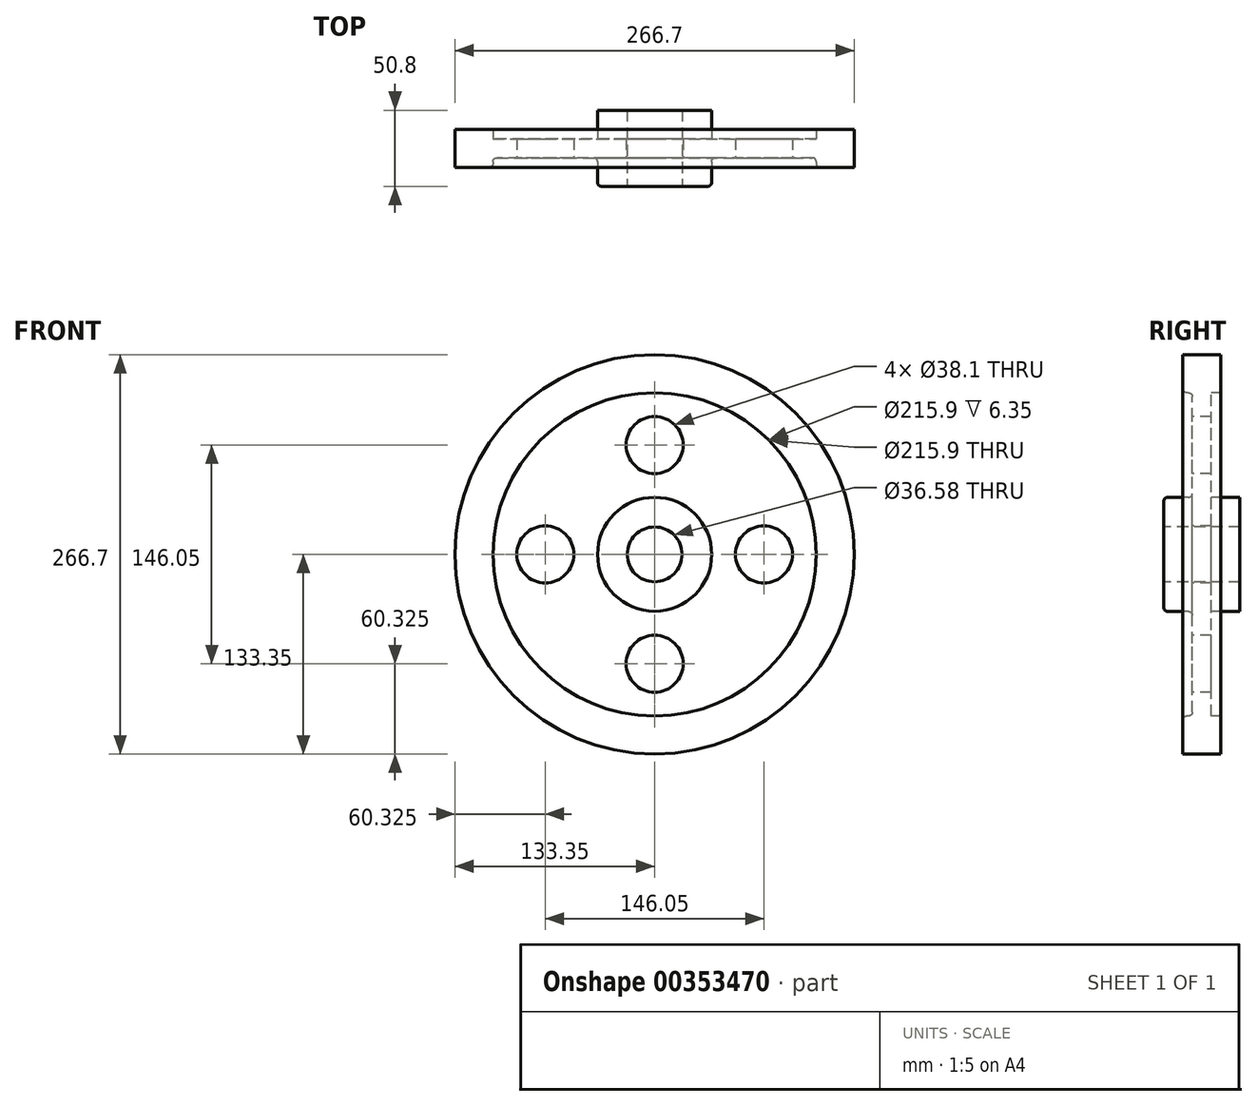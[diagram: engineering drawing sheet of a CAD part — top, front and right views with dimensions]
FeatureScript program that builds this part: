
annotation { "Feature Type Name" : "Feature", "Feature Type Description" : "" }
export const myFeature = defineFeature(function(context is Context, id is Id, definition is map)
    precondition{}
    {
        {
            var Q0;
            Q0=qCreatedBy(makeId("Right.planeOp"),FACE);
            var sketch = newSketch(context, id + "F0", { "sketchPlane" : qUnion([Q0])});
            skLineSegment(sketch, "E0", {"start": v(0, 0) * mm, "end": v(76.21, 0) * mm, "construction": true});
            skLineSegment(sketch, "E1.0", {"start": v(0, 18.29) * mm, "end": v(25.4, 18.29) * mm});
            skLineSegment(sketch, "E2.0", {"start": v(6.35, 38.1) * mm, "end": v(25.4, 38.1) * mm});
            skLineSegment(sketch, "E3.0", {"start": v(6.35, 107.95) * mm, "end": v(12.7, 107.95) * mm});
            skLineSegment(sketch, "E4.0", {"start": v(0, 133.35) * mm, "end": v(12.7, 133.35) * mm});
            skLineSegment(sketch, "E5", {"start": v(0, 0) * mm, "end": v(0, 133.35) * mm, "construction": true});
            skLineSegment(sketch, "E6.0", {"start": v(25.4, 18.29) * mm, "end": v(25.4, 38.1) * mm});
            skLineSegment(sketch, "E7.0", {"start": v(6.35, 38.1) * mm, "end": v(6.35, 107.95) * mm});
            skLineSegment(sketch, "E8.trimOffspring", {"start": v(12.7, 107.95) * mm, "end": v(12.7, 133.35) * mm});
            skLineSegment(sketch, "E9.MirrorCS", {"start": v(0, 133.35) * mm, "end": v(-12.7, 133.35) * mm});
            skLineSegment(sketch, "E10.MirrorCS", {"start": v(-12.7, 107.95) * mm, "end": v(-12.7, 133.35) * mm});
            skLineSegment(sketch, "E11.MirrorCS", {"start": v(-6.35, 107.95) * mm, "end": v(-12.7, 107.95) * mm});
            skLineSegment(sketch, "E12.MirrorCS", {"start": v(-6.35, 38.1) * mm, "end": v(-6.35, 107.95) * mm});
            skLineSegment(sketch, "E13.MirrorCS", {"start": v(-6.35, 38.1) * mm, "end": v(-25.4, 38.1) * mm});
            skLineSegment(sketch, "E14.MirrorCS", {"start": v(-25.4, 18.29) * mm, "end": v(-25.4, 38.1) * mm});
            skLineSegment(sketch, "E15.MirrorCS", {"start": v(0, 18.29) * mm, "end": v(-25.4, 18.29) * mm});
            skSolve(sketch);
        }
        {
            var Q0;
            Q0=makeQuery(id+"F0.imprint","IMPRINT",FACE,{"disambiguationData":[TD([[makeQuery(id+"F0.imprint","IMPRINT",EDGE,{"derivedFrom":sQuery(id+"F0.wireOp",EDGE,"E1.0")}),1.0]])]});
            var Q1;
            Q1=sQuery(id+"F0.wireOp",EDGE,"E0");
            revolve(context, id + "F1", {"entities" : qUnion([Q0]), "axis" : qUnion([Q1]), "revolveType" : RevolveType.FULL});
        }
        {
            var Q0;
            Q0=makeQuery(id+"F1.opRevolve","SWEPT_FACE",FACE,{"disambiguationData":[OSD([sQuery(id+"F0.wireOp",EDGE,"E12.MirrorCS")])]});
            var sketch = newSketch(context, id + "F2", { "sketchPlane" : qUnion([Q0])});
            skLineSegment(sketch, "E16", {"start": v(0, 0) * mm, "end": v(0, 73.03) * mm});
            skCircle(sketch, "E17", {"center": v(0, 73.03) * mm, "radius": 19.05 * mm});
            skCircle(sketch, "E18.1.0", {"center": v(-73.03, 0) * mm, "radius": 19.05 * mm});
            skCircle(sketch, "E18.2.0", {"center": v(0, -73.03) * mm, "radius": 19.05 * mm});
            skCircle(sketch, "E18.3.0", {"center": v(73.03, 0) * mm, "radius": 19.05 * mm});
            skPoint(sketch, "E18.center", {"position": v(0, 0) * mm});
            skSolve(sketch);
        }
        {
            var Q0;
            Q0=makeQuery(id+"F2.imprint","IMPRINT",FACE,{"disambiguationData":[TD([[makeQuery(id+"F2.imprint","IMPRINT",EDGE,{"derivedFrom":sQuery(id+"F2.wireOp",EDGE,"E17")}),1.0]])]});
            var Q1;
            Q1=makeQuery(id+"F2.imprint","IMPRINT",FACE,{"disambiguationData":[TD([[makeQuery(id+"F2.imprint","IMPRINT",EDGE,{"derivedFrom":sQuery(id+"F2.wireOp",EDGE,"E18.3.0")}),1.0]])]});
            var Q2;
            Q2=makeQuery(id+"F2.imprint","IMPRINT",FACE,{"disambiguationData":[TD([[makeQuery(id+"F2.imprint","IMPRINT",EDGE,{"derivedFrom":sQuery(id+"F2.wireOp",EDGE,"E18.1.0")}),1.0]])]});
            var Q3;
            Q3=makeQuery(id+"F2.imprint","IMPRINT",FACE,{"disambiguationData":[TD([[makeQuery(id+"F2.imprint","IMPRINT",EDGE,{"derivedFrom":sQuery(id+"F2.wireOp",EDGE,"E18.2.0")}),1.0]])]});
            extrude(context, id + "F3", {"entities" : qUnion([Q0, Q1, Q2, Q3]), "operationType" : NewBodyOperationType.REMOVE, "oppositeDirection" : true, "depth" : 25.4 * mm});
        }
        {
            var Q0;
            Q0=makeQuery(id+"F1.opRevolve","SWEPT_EDGE",EDGE,{"disambiguationData":[OSD([sQuery(id+"F0.wireOp",EDGE,"E13.MirrorCS"),sQuery(id+"F0.wireOp",EDGE,"E14.MirrorCS")])]});
            var Q1;
            Q1=makeQuery(id+"F1.opRevolve","SWEPT_EDGE",EDGE,{"disambiguationData":[OSD([sQuery(id+"F0.wireOp",EDGE,"E12.MirrorCS"),sQuery(id+"F0.wireOp",EDGE,"E13.MirrorCS")])]});
            var Q2;
            Q2=makeQuery(id+"F1.opRevolve","SWEPT_EDGE",EDGE,{"disambiguationData":[OSD([sQuery(id+"F0.wireOp",EDGE,"E10.MirrorCS"),sQuery(id+"F0.wireOp",EDGE,"E11.MirrorCS")])]});
            var Q3;
            Q3=makeQuery(id+"F1.opRevolve","SWEPT_EDGE",EDGE,{"disambiguationData":[OSD([sQuery(id+"F0.wireOp",EDGE,"E11.MirrorCS"),sQuery(id+"F0.wireOp",EDGE,"E12.MirrorCS")])]});
            fillet(context, id + "F4", {"entities" : qUnion([Q0, Q1, Q2, Q3]), "radius" : 2.54 * mm, "tangentPropagation" : true, "allowEdgeOverflow" : false});
        }
    });
